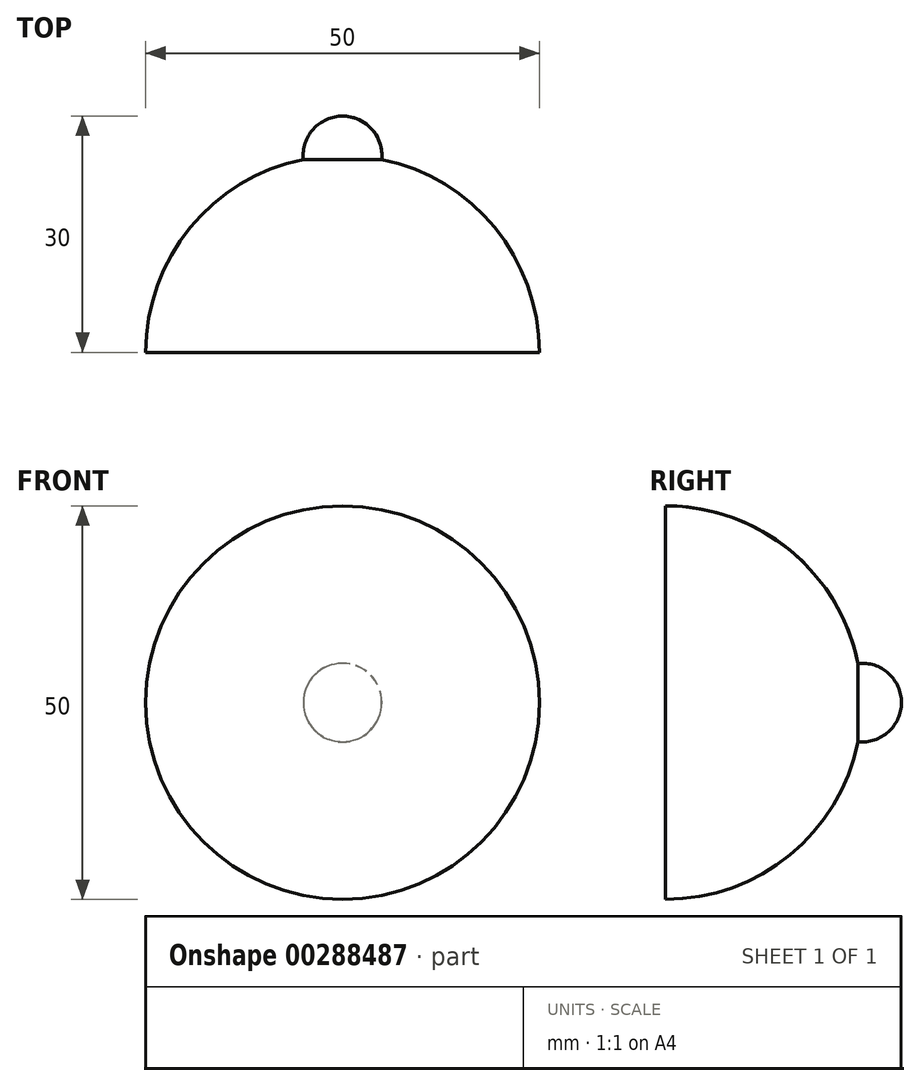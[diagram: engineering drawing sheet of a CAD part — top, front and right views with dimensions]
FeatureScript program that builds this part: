
annotation { "Feature Type Name" : "Feature", "Feature Type Description" : "" }
export const myFeature = defineFeature(function(context is Context, id is Id, definition is map)
    precondition{}
    {
        {
            var Q0;
            Q0=qCreatedBy(makeId("Top.planeOp"),FACE);
            var sketch = newSketch(context, id + "F0", { "sketchPlane" : qUnion([Q0])});
            skArc(sketch, "E0", {"start": v(25, 0) * mm, "mid": v(19.36, 15.82) * mm, "end": v(4.97, 24.5) * mm});
            skArc(sketch, "E1", {"start": v(4.97, 24.5) * mm, "mid": v(3.7, 28.35) * mm, "end": v(0, 30) * mm});
            skLineSegment(sketch, "E2", {"start": v(0, 25) * mm, "end": v(0, 0) * mm});
            skLineSegment(sketch, "E3", {"start": v(0, 0) * mm, "end": v(25, 0) * mm});
            skLineSegment(sketch, "E4", {"start": v(0, 85.33) * mm, "end": v(0, -68.3) * mm, "construction": true});
            skLineSegment(sketch, "E5", {"start": v(0, 30) * mm, "end": v(0, 0) * mm});
            skSolve(sketch);
        }
        {
            var Q0;
            Q0=makeQuery(id+"F0.imprint","IMPRINT",FACE,{"disambiguationData":[TD([[makeQuery(id+"F0.imprint","IMPRINT",EDGE,{"derivedFrom":sQuery(id+"F0.wireOp",EDGE,"E0")}),1.0]])]});
            var Q1;
            Q1=sQuery(id+"F0.wireOp",EDGE,"E4");
            revolve(context, id + "F1", {"entities" : qUnion([Q0]), "axis" : qUnion([Q1]), "revolveType" : RevolveType.FULL});
        }
    });
